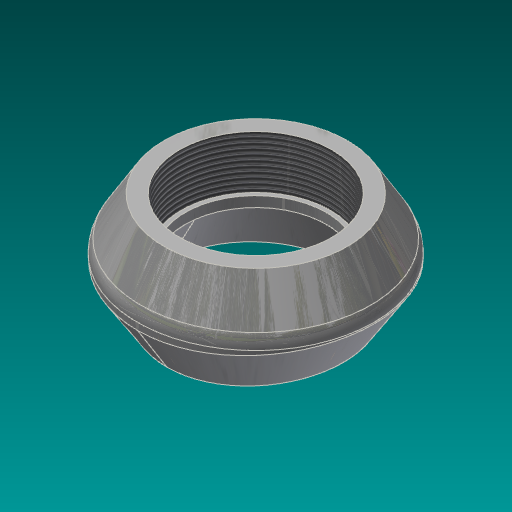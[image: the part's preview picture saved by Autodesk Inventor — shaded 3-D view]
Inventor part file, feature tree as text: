
AUTODESK INVENTOR PART (.ipt)
format: ipt  version: 2017.3 (Build 213257000, 257)  size: 448,000 bytes
history: native  units: mm (DEFAULTED — no unit token found)
features: other x8, sketch x5, plane x1, extrude x1, revolve x1, thread x1, sweep x1
ambient origin geometry x8: Origin, YZ Plane, XZ Plane, XY Plane, X Axis, Y Axis, Z Axis, Center Point
bodies: Solid1 (feature_tree)
feature tree (18):
  sketch  "Sketch1"  dims[d5=38.1mm d8=90.0deg]
  plane  "Work Plane1"
  sketch  "Sketch2"  dims[d9=0.0mm d10=866.775mm d11=10.0mm d12=0.0mm]
  extrude  "Extrusion1"  TaperAngle=90.0deg  [1 undecoded]
  revolve  "Revolution2"  [1 undecoded]
  thread  "Thread1"  [1 undecoded]
  other  "Work Point1"
  sweep  "Sweep1"
  other  "Work Axis3"
  other  "Work Point2"
  other  "Work Point3"
  sketch  "Sketch3"  dims[d45=8.810625mm d52=88.10625mm]
  sketch  "Sketch4"  dims[d54=1121.56875mm d77=68.1482mm d80=38.1mm d81=19.2151mm d83=56.55818mm d85=0.312398mm d86=90.0deg d91=52.5018mm d92=6.0mm d93=4.0mm d94=2.0mm d95=90.0deg d96=3.84302mm d97=0.0mm d102=10.0mm d103=0.0mm d106=19.05mm d107=471.4875mm d120=-433.3875mm d121=0.0mm d129=0.78232mm d130=0.78232mm d131=30.0deg d132=11.509375mm d133=0.0mm d134=0.0mm d135=90.0deg d136=0.0mm d137=90.0deg d138=65.0875mm d139=58.3692mm d140=0.0mm]
  other  "Work Axis2"
  sketch  "3D Sketch1"
  other  "Edges14"
  other  "Edges15"
  other  "Work Axis4"
note: 3 required parameter values undecoded (feature->parameter linkage not recoverable at this tier; creation-order binding heuristic only, values carry confidence <= 0.55)